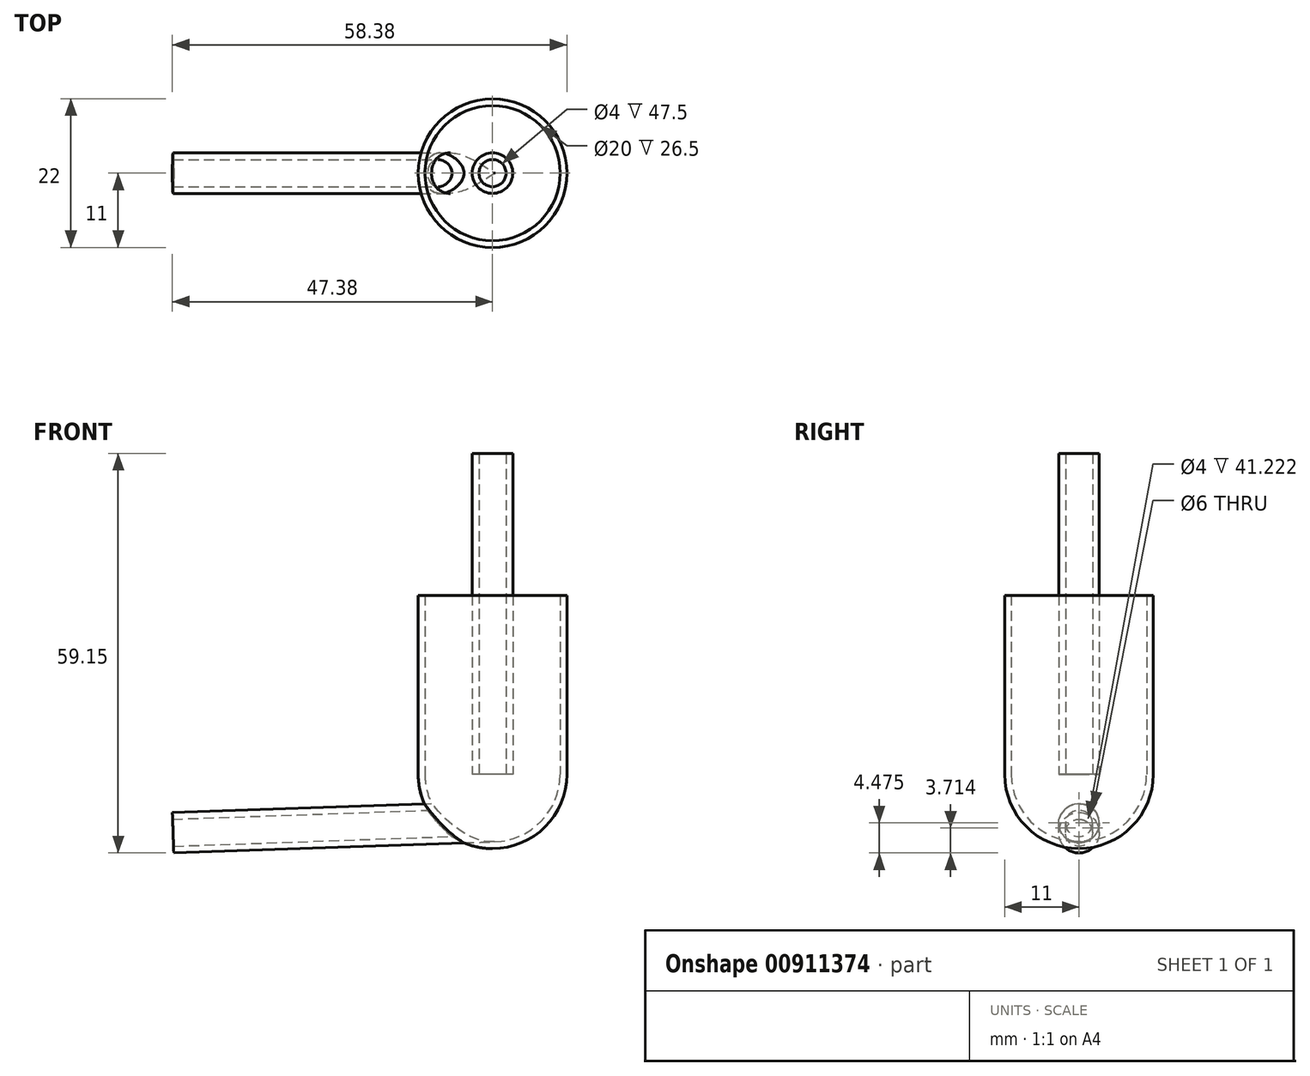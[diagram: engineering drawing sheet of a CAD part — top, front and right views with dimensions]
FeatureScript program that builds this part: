
annotation { "Feature Type Name" : "Feature", "Feature Type Description" : "" }
export const myFeature = defineFeature(function(context is Context, id is Id, definition is map)
    precondition{}
    {
        {
            var Q0;
            Q0=qCreatedBy(makeId("Front.planeOp"),FACE);
            var sketch = newSketch(context, id + "F0", { "sketchPlane" : qUnion([Q0])});
            skLineSegment(sketch, "E0.top", {"start": v(0, 26.5) * mm, "end": v(-11, 26.5) * mm});
            skLineSegment(sketch, "E0.left", {"start": v(0, 0) * mm, "end": v(0, 26.5) * mm});
            skLineSegment(sketch, "E0.right", {"start": v(-11, 0) * mm, "end": v(-11, 26.5) * mm});
            skLineSegment(sketch, "E1", {"start": v(0, -11) * mm, "end": v(0, 0) * mm});
            skArc(sketch, "E2", {"start": v(-11, 0) * mm, "mid": v(-7.78, -7.78) * mm, "end": v(0, -11) * mm});
            skLineSegment(sketch, "E3", {"start": v(0, 0) * mm, "end": v(-7.78, -7.78) * mm, "construction": true});
            skLineSegment(sketch, "E4", {"start": v(-7.78, -7.78) * mm, "end": v(-29.92, -8.55) * mm, "construction": true});
            skSolve(sketch);
        }
        {
            var Q0;
            Q0 = qSketchRegion(id + "F0", true);
            var Q1;
            Q1=sQuery(id+"F0.wireOp",EDGE,"E0.left");
            revolve(context, id + "F1", {"surfaceOperationType" : NewSurfaceOperationType.NEW, "entities" : qUnion([Q0]), "axis" : qUnion([Q1]), "revolveType" : RevolveType.FULL});
        }
        {
            var Q0;
            Q0=makeQuery(id+"F1.opRevolve","SWEPT_FACE",FACE,{"disambiguationData":[OSD([sQuery(id+"F0.wireOp",EDGE,"E0.top")])]});
            shell(context, id + "F2", {"entities" : qUnion([Q0]), "thickness" : 1 * mm});
        }
        {
            var Q0;
            Q0=qCreatedBy(makeId("Top.planeOp"),FACE);
            var sketch = newSketch(context, id + "F3", { "sketchPlane" : qUnion([Q0])});
            skCircle(sketch, "E5", {"center": v(0, 0) * mm, "radius": 2 * mm});
            skCircle(sketch, "E6", {"center": v(0, 0) * mm, "radius": 3 * mm});
            skSolve(sketch);
        }
        {
            var Q0;
            Q0 = qSketchRegion(id + "F3", true);
            extrude(context, id + "F4", {"entities" : qUnion([Q0]), "depth" : 47.5 * mm, "offsetDistance" : 25 * mm});
        }
        {
            var Q0;
            Q0=sQuery(id+"F0.wireOp",EDGE,"E2");
            cPoint(context, id + "F5", {"entities" : qUnion([Q0]), "parameter" : 0.5});
        }
        {
            var Q0;
            Q0=sQuery(id+"F0.wireOp",EDGE,"E4");
            var Q1;
            Q1 = qCreatedBy(id + "F5" ,VERTEX);
            cPlane(context, id + "F6", {"entities" : qUnion([Q0, Q1]), "cplaneType" : CPlaneType.LINE_POINT, "offset" : 25 * mm, "width" : 150 * mm, "height" : 150 * mm});
        }
        {
            var Q0;
            Q0=qCreatedBy(id+"F6.planeOp",FACE);
            cPlane(context, id + "F7", {"entities" : qUnion([Q0]), "cplaneType" : CPlaneType.OFFSET, "offset" : 8 * mm, "oppositeDirection" : true, "width" : 150 * mm, "height" : 150 * mm});
        }
        {
            var Q0;
            Q0=qCreatedBy(id+"F7.planeOp",FACE);
            var sketch = newSketch(context, id + "F8", { "sketchPlane" : qUnion([Q0])});
            skCircle(sketch, "E7", {"center": v(0, -7) * mm, "radius": 3 * mm});
            skSolve(sketch);
        }
        {
            var Q0;
            Q0 = qSketchRegion(id + "F8", true);
            extrude(context, id + "F9", {"entities" : qUnion([Q0]), "depth" : 47.5 * mm, "offsetDistance" : 25 * mm});
        }
        {
            var Q0;
            Q0=makeQuery(id+"F9.opExtrude","SWEPT_BODY",BODY,{"disambiguationData":[OSD([sQuery(id+"F8.wireOp",EDGE,"E7"),sQuery(id+"F8.wireOp",EDGE,"dqexc5W7-ZmaL-oUg1-WgDL-rl6ny0AZS6zH")])]});
            var Q1;
            Q1=makeQuery(id+"F1.opRevolve","SWEPT_BODY",BODY,{"disambiguationData":[OSD([sQuery(id+"F0.wireOp",EDGE,"E0.top"),sQuery(id+"F0.wireOp",EDGE,"E0.left"),sQuery(id+"F0.wireOp",EDGE,"E0.right"),sQuery(id+"F0.wireOp",EDGE,"E1"),sQuery(id+"F0.wireOp",EDGE,"E2")])]});
            booleanBodies(context, id + "F10", {"operationType" : BooleanOperationType.SUBTRACTION, "tools" : qUnion([Q0]), "targets" : qUnion([Q1]), "keepTools" : true});
        }
        {
            var Q0;
            Q0 = qSketchRegion(id + "F0", true);
            var Q1;
            Q1=sQuery(id+"F0.wireOp",EDGE,"E0.left");
            revolve(context, id + "F11", {"surfaceOperationType" : NewSurfaceOperationType.NEW, "entities" : qUnion([Q0]), "axis" : qUnion([Q1]), "revolveType" : RevolveType.FULL});
        }
        {
            var Q0;
            Q0=makeQuery(id+"F11.opRevolve","SWEPT_BODY",BODY,{"disambiguationData":[OSD([sQuery(id+"F0.wireOp",EDGE,"E0.top"),sQuery(id+"F0.wireOp",EDGE,"E0.left"),sQuery(id+"F0.wireOp",EDGE,"E0.right"),sQuery(id+"F0.wireOp",EDGE,"E1"),sQuery(id+"F0.wireOp",EDGE,"E2")])]});
            var Q1;
            Q1=makeQuery(id+"F9.opExtrude","SWEPT_BODY",BODY,{"disambiguationData":[OSD([sQuery(id+"F8.wireOp",EDGE,"E7")])]});
            booleanBodies(context, id + "F12", {"operationType" : BooleanOperationType.SUBTRACTION, "tools" : qUnion([Q0]), "targets" : qUnion([Q1])});
        }
        {
            var Q0;
            Q0=makeQuery(id+"F9.opExtrude","CAP_FACE",FACE,{"disambiguationData":[OSD([sQuery(id+"F8.wireOp",EDGE,"E7")])],"isStart":false});
            var Q1;
            Q1=makeQuery(id+"F12.opBoolean","COPY",FACE,{"derivedFrom":makeQuery(id+"F11.opRevolve","SWEPT_FACE",FACE,{"disambiguationData":[OSD([sQuery(id+"F0.wireOp",EDGE,"E2")])]})});
            shell(context, id + "F13", {"entities" : qUnion([Q0, Q1]), "thickness" : 1 * mm});
        }
    });
